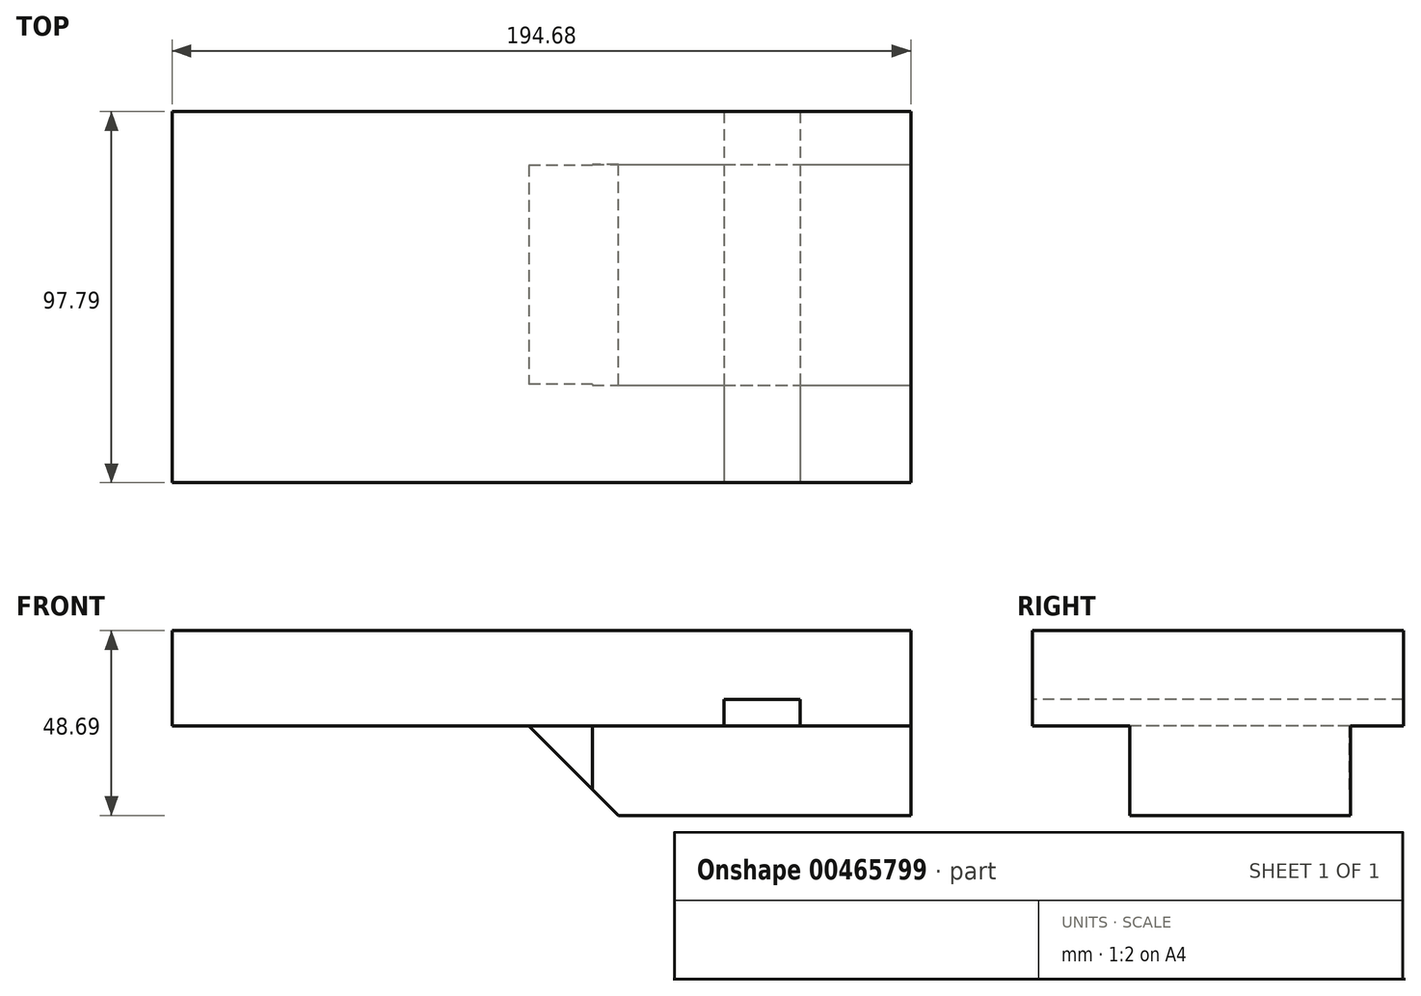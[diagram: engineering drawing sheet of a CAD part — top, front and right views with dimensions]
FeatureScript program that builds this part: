
annotation { "Feature Type Name" : "Feature", "Feature Type Description" : "" }
export const myFeature = defineFeature(function(context is Context, id is Id, definition is map)
    precondition{}
    {
        {
            var Q0;
            Q0=qCreatedBy(makeId("Front.planeOp"),FACE);
            var sketch = newSketch(context, id + "F0", { "sketchPlane" : qUnion([Q0])});
            skLineSegment(sketch, "E0.bottom", {"start": v(-92.18, 14.56) * mm, "end": v(102.5, 14.56) * mm});
            skLineSegment(sketch, "E0.top", {"start": v(-92.18, -10.5) * mm, "end": v(102.5, -10.5) * mm});
            skLineSegment(sketch, "E0.left", {"start": v(-92.18, 14.56) * mm, "end": v(-92.18, -10.5) * mm});
            skLineSegment(sketch, "E0.right", {"start": v(102.5, 14.56) * mm, "end": v(102.5, -10.5) * mm});
            skLineSegment(sketch, "E1.bottom", {"start": v(102.5, -10.5) * mm, "end": v(11.06, -10.5) * mm});
            skLineSegment(sketch, "E1.top", {"start": v(102.5, -27.65) * mm, "end": v(11.06, -27.65) * mm});
            skLineSegment(sketch, "E1.left", {"start": v(102.5, -10.5) * mm, "end": v(102.5, -27.65) * mm});
            skLineSegment(sketch, "E1.right", {"start": v(11.06, -10.5) * mm, "end": v(11.06, -27.65) * mm});
            skLineSegment(sketch, "E2.bottom", {"start": v(53.28, 3.5) * mm, "end": v(73.37, 3.5) * mm});
            skLineSegment(sketch, "E2.top", {"start": v(53.28, -10.5) * mm, "end": v(73.37, -10.5) * mm});
            skLineSegment(sketch, "E2.left", {"start": v(53.28, 3.5) * mm, "end": v(53.28, -10.5) * mm});
            skLineSegment(sketch, "E2.right", {"start": v(73.37, 3.5) * mm, "end": v(73.37, -10.5) * mm});
            skLineSegment(sketch, "E3", {"start": v(-76.14, 14.56) * mm, "end": v(-76.14, -10.5) * mm});
            skLineSegment(sketch, "E4", {"start": v(85.36, 14.56) * mm, "end": v(85.36, -10.5) * mm});
            skLineSegment(sketch, "E5", {"start": v(53.28, -3.5) * mm, "end": v(73.37, -3.5) * mm});
            skSolve(sketch);
        }
        {
            var Q0;
            {var subQ0=sQuery(id+"F0.wireOp",EDGE,"E0.left");Q0=makeQuery(id+"F0.imprint","IMPRINT",FACE,{"disambiguationData":[TD([[makeQuery(id+"F0.imprint","IMPRINT",EDGE,{"derivedFrom":subQ0}),1.0]])]});}
            var Q1;
            {var subQ0=sQuery(id+"F0.wireOp",EDGE,"E0.right");Q1=makeQuery(id+"F0.imprint","IMPRINT",FACE,{"disambiguationData":[TD([[makeQuery(id+"F0.imprint","IMPRINT",EDGE,{"derivedFrom":subQ0}),-1.0]])]});}
            var Q2;
            {var subQ6=sQuery(id+"F0.wireOp",EDGE,"E2.bottom");Q2=makeQuery(id+"F0.imprint","IMPRINT",FACE,{"disambiguationData":[TD([[makeQuery(id+"F0.imprint","IMPRINT",EDGE,{"derivedFrom":subQ6}),1.0]])]});}
            var Q3;
            {var subQ0=sQuery(id+"F0.wireOp",EDGE,"E2.bottom");Q3=makeQuery(id+"F0.imprint","IMPRINT",FACE,{"disambiguationData":[TD([[makeQuery(id+"F0.imprint","IMPRINT",EDGE,{"derivedFrom":subQ0}),-1.0]])]});}
            var Q4;
            {var subQ0=sQuery(id+"F0.wireOp",EDGE,"E2.top");Q4=makeQuery(id+"F0.imprint","IMPRINT",FACE,{"disambiguationData":[TD([[makeQuery(id+"F0.imprint","IMPRINT",EDGE,{"derivedFrom":subQ0}),1.0]])]});}
            extrude(context, id + "F1", {"entities" : qUnion([Q0, Q1, Q2, Q3, Q4]), "oppositeDirection" : true, "depth" : 97.8 * mm});
        }
        {
            var Q0;
            Q0=makeQuery(id+"F1.opExtrude","SWEPT_FACE",FACE,{"disambiguationData":[OSD([sQuery(id+"F0.wireOp",EDGE,"E0.top"),sQuery(id+"F0.wireOp",EDGE,"E1.bottom"),sQuery(id+"F0.wireOp",EDGE,"E2.top")])]});
            var sketch = newSketch(context, id + "F2", { "sketchPlane" : qUnion([Q0])});
            skLineSegment(sketch, "E6.right", {"start": v(102.5, -25.74) * mm, "end": v(102.5, -83.83) * mm});
            skLineSegment(sketch, "E7", {"start": v(18.63, -25.74) * mm, "end": v(18.63, -83.83) * mm});
            skLineSegment(sketch, "E8", {"start": v(18.63, -25.74) * mm, "end": v(102.5, -25.74) * mm});
            skLineSegment(sketch, "E9", {"start": v(18.63, -83.83) * mm, "end": v(102.5, -83.83) * mm});
            skSolve(sketch);
        }
        {
            var Q0;
            Q0=makeQuery(id+"F1.opExtrude","SWEPT_FACE",FACE,{"disambiguationData":[OSD([sQuery(id+"F0.wireOp",EDGE,"E0.top"),sQuery(id+"F0.wireOp",EDGE,"E1.bottom"),sQuery(id+"F0.wireOp",EDGE,"E2.top")])]});
            var sketch = newSketch(context, id + "F3", { "sketchPlane" : qUnion([Q0])});
            skSolve(sketch);
        }
        {
            var Q0;
            Q0 = qSketchRegion(id + "F2", true);
            extrude(context, id + "F4", {"entities" : qUnion([Q0]), "operationType" : NewBodyOperationType.ADD, "depth" : 23.62 * mm});
        }
        {
            var Q0;
            {var subQ0=sQuery(id+"F0.wireOp",EDGE,"E0.top");Q0=makeQuery(id+"F3.imprint","IMPRINT",FACE,{"disambiguationData":[TD([[makeQuery(id+"F3.imprint","IMPRINT",EDGE,{"derivedFrom":makeQuery(id+"F1.opExtrude","SWEPT_EDGE",EDGE,{"disambiguationData":[OSD([subQ0,sQuery(id+"F0.wireOp",EDGE,"E0.left")])]})}),-1.0]])]});}
            var sketch = newSketch(context, id + "F5", { "sketchPlane" : qUnion([Q0])});
            skLineSegment(sketch, "E10.bottom", {"start": v(18.63, -25.95) * mm, "end": v(0, -25.95) * mm});
            skLineSegment(sketch, "E10.top", {"start": v(18.63, -83.62) * mm, "end": v(0, -83.62) * mm});
            skLineSegment(sketch, "E10.left", {"start": v(18.63, -25.95) * mm, "end": v(18.63, -83.62) * mm});
            skLineSegment(sketch, "E10.right", {"start": v(0, -25.95) * mm, "end": v(0, -83.62) * mm});
            skSolve(sketch);
        }
        {
            var Q0;
            Q0 = qSketchRegion(id + "F5", true);
            extrude(context, id + "F6", {"entities" : qUnion([Q0]), "operationType" : NewBodyOperationType.ADD, "depth" : 23.62 * mm});
        }
        {
            var Q0;
            Q0=makeQuery(id+"F6.opExtrude","CAP_EDGE",EDGE,{"disambiguationData":[OSD([sQuery(id+"F5.wireOp",EDGE,"E10.right")])],"isStart":false});
            chamfer(context, id + "F7", {"entities" : qUnion([Q0]), "width" : 25.4 * mm, "tangentPropagation" : true});
        }
    });
